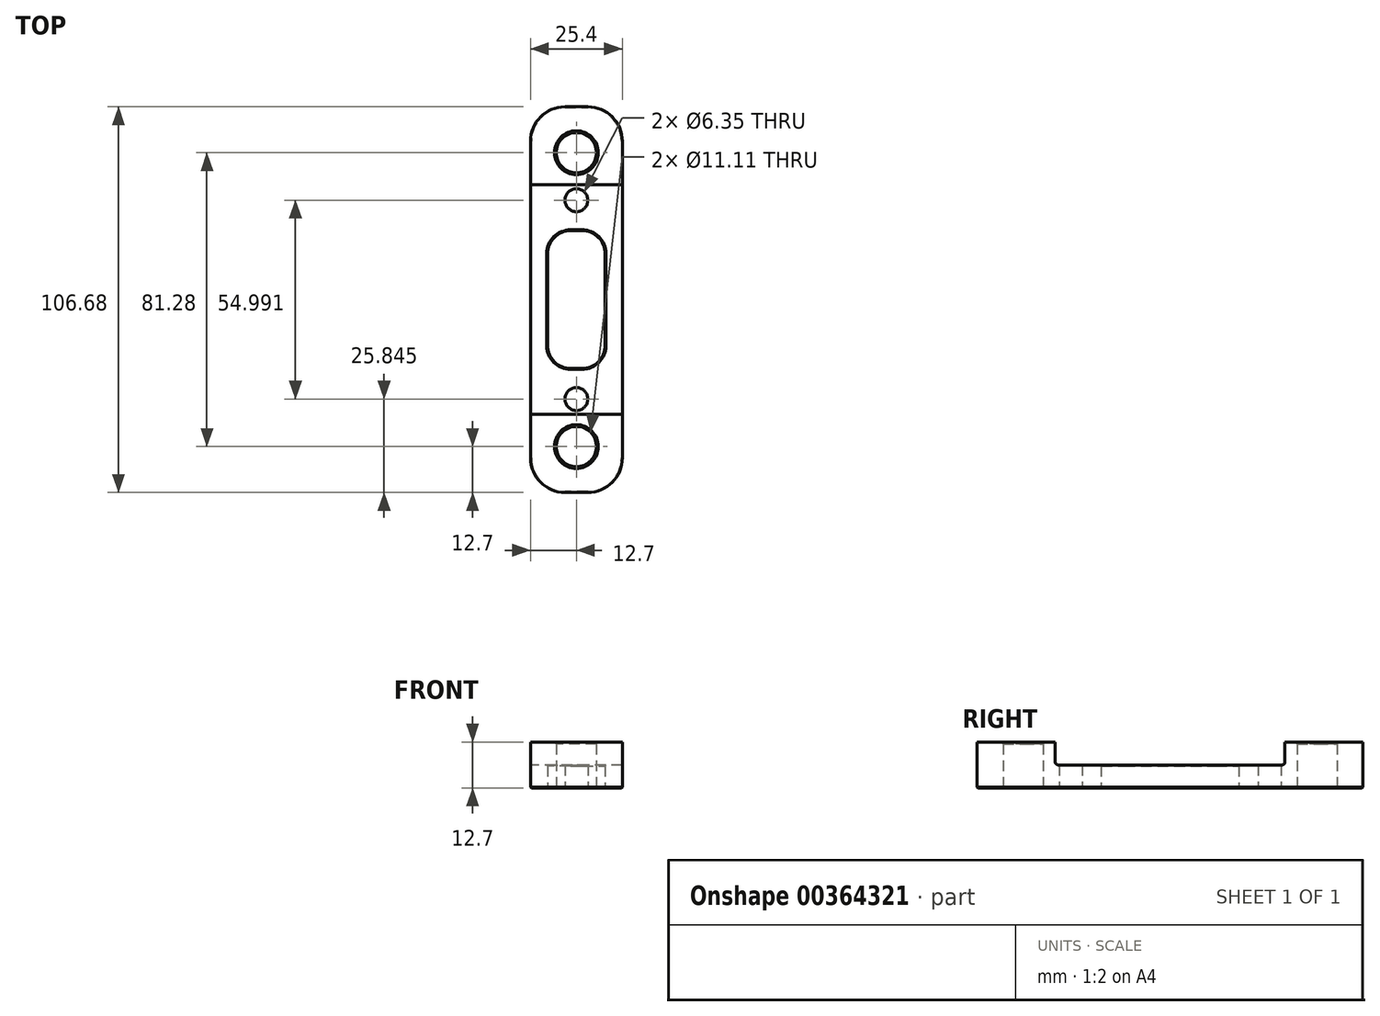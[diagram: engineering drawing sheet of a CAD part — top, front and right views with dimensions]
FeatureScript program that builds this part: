
annotation { "Feature Type Name" : "Feature", "Feature Type Description" : "" }
export const myFeature = defineFeature(function(context is Context, id is Id, definition is map)
    precondition{}
    {
        {
            var Q0;
            Q0=qCreatedBy(makeId("Top.planeOp"),FACE);
            var sketch = newSketch(context, id + "F0", { "sketchPlane" : qUnion([Q0])});
            skLineSegment(sketch, "E0.bottom", {"start": v(25.4, 106.68) * mm, "end": v(0, 106.68) * mm});
            skLineSegment(sketch, "E0.top", {"start": v(25.4, 0) * mm, "end": v(0, 0) * mm});
            skLineSegment(sketch, "E0.left", {"start": v(25.4, 106.68) * mm, "end": v(25.4, 0) * mm});
            skLineSegment(sketch, "E0.right", {"start": v(0, 106.68) * mm, "end": v(0, 0) * mm});
            skSolve(sketch);
        }
        {
            var Q0;
            Q0=qSketchRegion(id+"F0",true);
            extrude(context, id + "F1", {"entities" : qUnion([Q0]), "depth" : 12.7 * mm});
        }
        {
            var Q0;
            Q0=qCreatedBy(makeId("Right.planeOp"),FACE);
            var sketch = newSketch(context, id + "F2", { "sketchPlane" : qUnion([Q0])});
            skLineSegment(sketch, "E1.bottom", {"start": v(22.38, 6.35) * mm, "end": v(84.3, 6.35) * mm});
            skLineSegment(sketch, "E1.top", {"start": v(21.59, 19.05) * mm, "end": v(85.1, 19.05) * mm});
            skLineSegment(sketch, "E1.left", {"start": v(21.59, 7.14) * mm, "end": v(21.59, 19.05) * mm});
            skLineSegment(sketch, "E1.right", {"start": v(85.1, 7.14) * mm, "end": v(85.1, 19.05) * mm});
            skPoint(sketch, "E2.visualSharp", {"position": v(21.59, 6.35) * mm});
            skArc(sketch, "E2.filletArc", {"start": v(21.59, 7.14) * mm, "mid": v(21.82, 6.58) * mm, "end": v(22.38, 6.35) * mm});
            skPoint(sketch, "E3.visualSharp", {"position": v(85.1, 6.35) * mm});
            skArc(sketch, "E3.filletArc", {"start": v(84.3, 6.35) * mm, "mid": v(84.86, 6.58) * mm, "end": v(85.1, 7.14) * mm});
            skSolve(sketch);
        }
        {
            var Q0;
            Q0=qSketchRegion(id+"F2",true);
            extrude(context, id + "F3", {"entities" : qUnion([Q0]), "operationType" : NewBodyOperationType.REMOVE, "depth" : 27.94 * mm});
        }
        {
            var Q0;
            Q0=qCreatedBy(makeId("Top.planeOp"),FACE);
            var sketch = newSketch(context, id + "F4", { "sketchPlane" : qUnion([Q0])});
            skCircle(sketch, "E4", {"center": v(12.7, 80.84) * mm, "radius": 3.18 * mm});
            skCircle(sketch, "E5", {"center": v(12.7, 25.84) * mm, "radius": 3.18 * mm});
            skSolve(sketch);
        }
        {
            var Q0;
            Q0=qSketchRegion(id+"F4",true);
            extrude(context, id + "F5", {"entities" : qUnion([Q0]), "operationType" : NewBodyOperationType.REMOVE, "depth" : 25.4 * mm});
        }
        {
            var Q0;
            Q0=qCreatedBy(makeId("Top.planeOp"),FACE);
            var sketch = newSketch(context, id + "F6", { "sketchPlane" : qUnion([Q0])});
            skCircle(sketch, "E6", {"center": v(12.7, 93.98) * mm, "radius": 5.56 * mm});
            skCircle(sketch, "E7", {"center": v(12.7, 12.7) * mm, "radius": 5.56 * mm});
            skSolve(sketch);
        }
        {
            var Q0;
            Q0=qSketchRegion(id+"F6",true);
            extrude(context, id + "F7", {"entities" : qUnion([Q0]), "operationType" : NewBodyOperationType.REMOVE, "depth" : 25.4 * mm});
        }
        {
            var Q0;
            Q0=qCreatedBy(makeId("Top.planeOp"),FACE);
            var sketch = newSketch(context, id + "F8", { "sketchPlane" : qUnion([Q0])});
            skLineSegment(sketch, "E8.bottom", {"start": v(11.11, 72.4) * mm, "end": v(14.29, 72.4) * mm});
            skLineSegment(sketch, "E8.top", {"start": v(11.11, 34.3) * mm, "end": v(14.29, 34.3) * mm});
            skLineSegment(sketch, "E8.left", {"start": v(4.76, 66.04) * mm, "end": v(4.76, 40.64) * mm});
            skLineSegment(sketch, "E8.right", {"start": v(20.64, 66.04) * mm, "end": v(20.64, 40.64) * mm});
            skPoint(sketch, "E9.visualSharp", {"position": v(4.76, 34.3) * mm});
            skArc(sketch, "E9.filletArc", {"start": v(4.76, 40.64) * mm, "mid": v(6.62, 36.15) * mm, "end": v(11.11, 34.3) * mm});
            skPoint(sketch, "E10.visualSharp", {"position": v(20.64, 34.3) * mm});
            skArc(sketch, "E10.filletArc", {"start": v(14.29, 34.3) * mm, "mid": v(18.78, 36.15) * mm, "end": v(20.64, 40.64) * mm});
            skPoint(sketch, "E11.visualSharp", {"position": v(20.64, 72.4) * mm});
            skArc(sketch, "E11.filletArc", {"start": v(20.64, 66.04) * mm, "mid": v(18.78, 70.53) * mm, "end": v(14.29, 72.4) * mm});
            skPoint(sketch, "E12.visualSharp", {"position": v(4.76, 72.4) * mm});
            skArc(sketch, "E12.filletArc", {"start": v(11.11, 72.4) * mm, "mid": v(6.62, 70.53) * mm, "end": v(4.76, 66.04) * mm});
            skSolve(sketch);
        }
        {
            var Q0;
            Q0=qSketchRegion(id+"F8",true);
            extrude(context, id + "F9", {"entities" : qUnion([Q0]), "operationType" : NewBodyOperationType.REMOVE, "depth" : 25.4 * mm});
        }
        {
            var Q0;
            Q0=makeQuery(id+"F7.boolean.opBoolean","COPY",EDGE,{"derivedFrom":makeQuery(id+"F7.opExtrude","CAP_EDGE",EDGE,{"disambiguationData":[OSD([sQuery(id+"F6.wireOp",EDGE,"E7")])],"isStart":true})});
            var Q1;
            Q1=makeQuery(id+"F7.boolean.opBoolean","COPY",EDGE,{"derivedFrom":makeQuery(id+"F7.opExtrude","CAP_EDGE",EDGE,{"disambiguationData":[OSD([sQuery(id+"F6.wireOp",EDGE,"E6")])],"isStart":true})});
            var Q2;
            Q2=makeQuery(id+"F5.boolean.opBoolean","COPY",EDGE,{"derivedFrom":makeQuery(id+"F5.opExtrude","CAP_EDGE",EDGE,{"disambiguationData":[OSD([sQuery(id+"F4.wireOp",EDGE,"E4")])],"isStart":true})});
            var Q3;
            Q3=makeQuery(id+"F5.boolean.opBoolean","COPY",EDGE,{"derivedFrom":makeQuery(id+"F5.opExtrude","CAP_EDGE",EDGE,{"disambiguationData":[OSD([sQuery(id+"F4.wireOp",EDGE,"E5")])],"isStart":true})});
            var Q4;
            {var subQ0=sQuery(id+"F0.wireOp",EDGE,"E0.bottom");var subQ1=sQuery(id+"F0.wireOp",EDGE,"E0.right");var subQ2=sQuery(id+"F0.wireOp",EDGE,"E0.left");Q4=makeQuery(id+"F7.boolean.opBoolean","INTERSECT",EDGE,{"derivedFrom":[makeQuery(id+"F3.boolean.opBoolean","SPLIT",FACE,{"disambiguationData":[TD([makeQuery(id+"F1.opExtrude","SWEPT_FACE",FACE,{"disambiguationData":[OSD([subQ0])]})])],"derivedFrom":makeQuery(id+"F1.opExtrude","CAP_FACE",FACE,{"disambiguationData":[OSD([subQ0,sQuery(id+"F0.wireOp",EDGE,"E0.top"),subQ2,subQ1])],"isStart":false})}),makeQuery(id+"F7.opExtrude","SWEPT_FACE",FACE,{"disambiguationData":[OSD([sQuery(id+"F6.wireOp",EDGE,"E6")])]})]});}
            var Q5;
            {var subQ0=sQuery(id+"F0.wireOp",EDGE,"E0.top");var subQ1=sQuery(id+"F0.wireOp",EDGE,"E0.left");var subQ2=sQuery(id+"F0.wireOp",EDGE,"E0.right");Q5=makeQuery(id+"F7.boolean.opBoolean","INTERSECT",EDGE,{"derivedFrom":[makeQuery(id+"F3.boolean.opBoolean","SPLIT",FACE,{"disambiguationData":[TD([makeQuery(id+"F1.opExtrude","SWEPT_FACE",FACE,{"disambiguationData":[OSD([subQ0])]})])],"derivedFrom":makeQuery(id+"F1.opExtrude","CAP_FACE",FACE,{"disambiguationData":[OSD([sQuery(id+"F0.wireOp",EDGE,"E0.bottom"),subQ0,subQ1,subQ2])],"isStart":false})}),makeQuery(id+"F7.opExtrude","SWEPT_FACE",FACE,{"disambiguationData":[OSD([sQuery(id+"F6.wireOp",EDGE,"E7")])]})]});}
            chamfer(context, id + "F10", {"entities" : qUnion([Q0, Q1, Q2, Q3, Q4, Q5]), "width" : 0.5 * mm, "tangentPropagation" : true});
        }
        {
            var Q0;
            Q0=makeQuery(id+"F9.boolean.opBoolean","COPY",EDGE,{"derivedFrom":makeQuery(id+"F9.opExtrude","CAP_EDGE",EDGE,{"disambiguationData":[OSD([sQuery(id+"F8.wireOp",EDGE,"E8.left")])],"isStart":true})});
            var Q1;
            Q1=makeQuery(id+"F9.boolean.opBoolean","INTERSECT",EDGE,{"derivedFrom":[makeQuery(id+"F3.boolean.opBoolean","COPY",FACE,{"derivedFrom":makeQuery(id+"F3.opExtrude","SWEPT_FACE",FACE,{"disambiguationData":[OSD([sQuery(id+"F2.wireOp",EDGE,"E1.bottom")])]})}),makeQuery(id+"F9.opExtrude","SWEPT_FACE",FACE,{"disambiguationData":[OSD([sQuery(id+"F8.wireOp",EDGE,"E8.right")])]})]});
            chamfer(context, id + "F11", {"entities" : qUnion([Q0, Q1]), "width" : 0.25 * mm, "tangentPropagation" : true});
        }
        {
            var Q0;
            Q0=makeQuery(id+"F1.opExtrude","SWEPT_EDGE",EDGE,{"disambiguationData":[OSD([sQuery(id+"F0.wireOp",EDGE,"E0.top"),sQuery(id+"F0.wireOp",EDGE,"E0.left")])]});
            var Q1;
            Q1=makeQuery(id+"F1.opExtrude","SWEPT_EDGE",EDGE,{"disambiguationData":[OSD([sQuery(id+"F0.wireOp",EDGE,"E0.top"),sQuery(id+"F0.wireOp",EDGE,"E0.right")])]});
            var Q2;
            Q2=makeQuery(id+"F1.opExtrude","SWEPT_EDGE",EDGE,{"disambiguationData":[OSD([sQuery(id+"F0.wireOp",EDGE,"E0.bottom"),sQuery(id+"F0.wireOp",EDGE,"E0.left")])]});
            var Q3;
            Q3=makeQuery(id+"F1.opExtrude","SWEPT_EDGE",EDGE,{"disambiguationData":[OSD([sQuery(id+"F0.wireOp",EDGE,"E0.bottom"),sQuery(id+"F0.wireOp",EDGE,"E0.right")])]});
            fillet(context, id + "F12", {"entities" : qUnion([Q0, Q1, Q2, Q3]), "radius" : 9.52 * mm, "tangentPropagation" : true, "allowEdgeOverflow" : false});
        }
        {
            var Q0;
            Q0=makeQuery(id+"F1.opExtrude","CAP_EDGE",EDGE,{"disambiguationData":[OSD([sQuery(id+"F0.wireOp",EDGE,"E0.right")])],"isStart":true});
            chamfer(context, id + "F13", {"entities" : qUnion([Q0]), "width" : 0.25 * mm, "tangentPropagation" : true});
        }
    });
